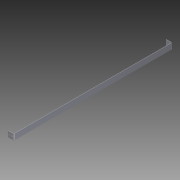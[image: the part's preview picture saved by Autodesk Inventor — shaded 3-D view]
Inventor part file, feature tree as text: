
AUTODESK INVENTOR PART (.ipt)
format: ipt  version: 2014 SP1 (Build 180222100, 222)  size: 125,952 bytes
history: native  units: in
note: dims shown in document units (in); Inventor stores cm internally (conversion verified against a paired STEP export)
features: sketch x4, extrude x3, sheet_metal_op x3, mirror x1, other x1
ambient origin geometry x8: Origin, YZ Plane, XZ Plane, XY Plane, X Axis, Y Axis, Z Axis, Center Point
bodies: Solid1 (feature_tree)
feature tree (12):
  extrude  "Extrusion1"  Depth=0.75in
  extrude  "Extrusion2"  Depth=0.0312in TaperAngle=0.0deg
  sheet_metal_op  "Flange1"
  extrude  "Extrusion3"  Depth=0.0312in
  mirror  "Mirror1"
  sketch  "Sketch1"  dims[d0=0.75in d1=0.75in]
  sketch  "Sketch2"  dims[d2=0.0312in d3=10.25in d4=0.0in]
  sketch  "Sketch3"  dims[d5=0.125in d6=0.0in d7=0.0312in]
  other  "Plate1"
  sheet_metal_op  "Bend1"
  sheet_metal_op  "Corner1"
  sketch  "Sketch4"  dims[d8=0.0156in d9=0.0625in d10=0.0312in d11=0.75in d12=90.0deg d13=0.025in d14=0.125in d15=0.0312in d16=0.0312in d19=0.125in d20=0.0in d21=0.125in d22=0.3125in]
